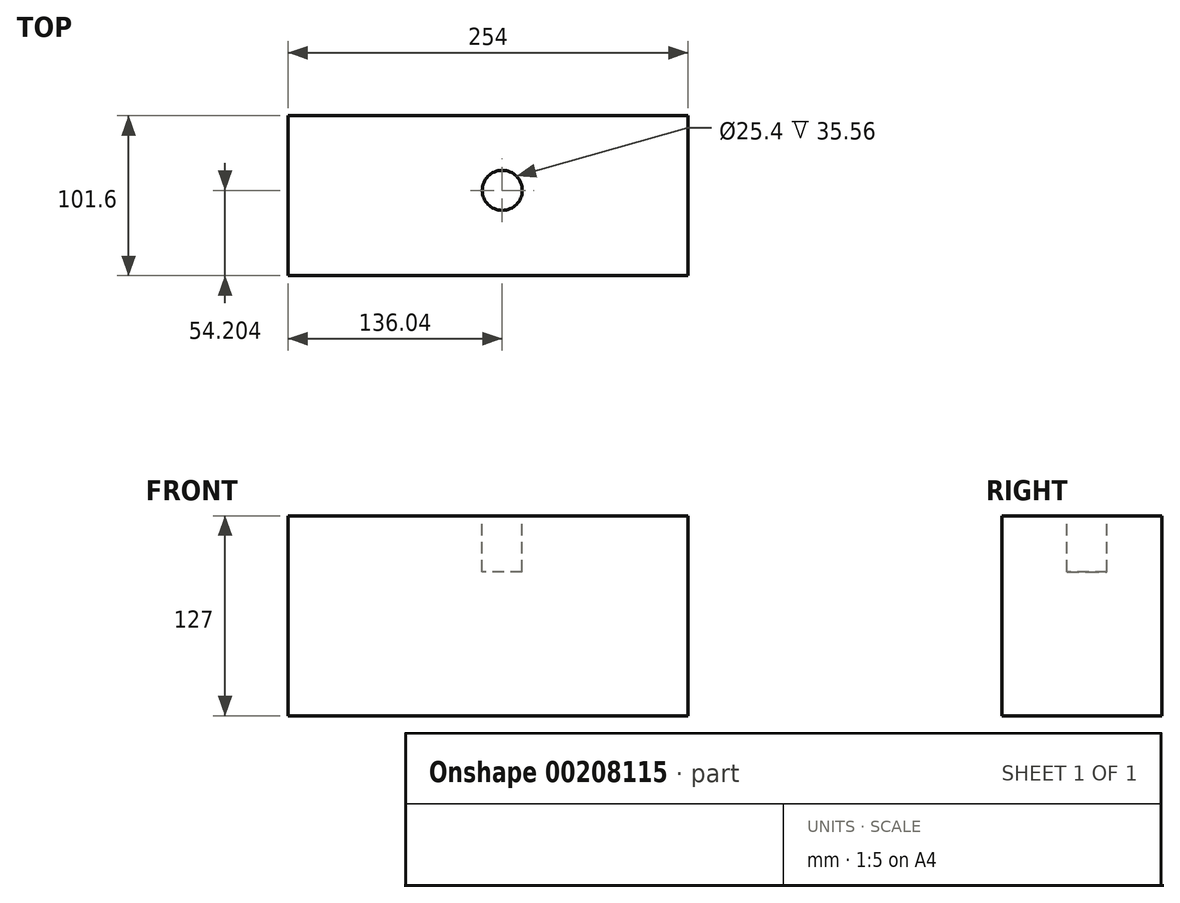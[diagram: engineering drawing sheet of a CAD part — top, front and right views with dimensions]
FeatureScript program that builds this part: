
annotation { "Feature Type Name" : "Feature", "Feature Type Description" : "" }
export const myFeature = defineFeature(function(context is Context, id is Id, definition is map)
    precondition{}
    {
        {
            var Q0;
            Q0=qCreatedBy(makeId("Top.planeOp"),FACE);
            var sketch = newSketch(context, id + "F0", { "sketchPlane" : qUnion([Q0])});
            skLineSegment(sketch, "E0.bottom", {"start": v(-214.22, -77.26) * mm, "end": v(39.78, -77.26) * mm});
            skLineSegment(sketch, "E0.top", {"start": v(-214.22, -178.86) * mm, "end": v(39.78, -178.86) * mm});
            skLineSegment(sketch, "E0.left", {"start": v(-214.22, -77.26) * mm, "end": v(-214.22, -178.86) * mm});
            skLineSegment(sketch, "E0.right", {"start": v(39.78, -77.26) * mm, "end": v(39.78, -178.86) * mm});
            skLineSegment(sketch, "E1.bottom", {"start": v(-9.04, 73.66) * mm, "end": v(41.76, 73.66) * mm});
            skLineSegment(sketch, "E1.top", {"start": v(-9.04, 200.66) * mm, "end": v(41.76, 200.66) * mm});
            skLineSegment(sketch, "E1.left", {"start": v(-9.04, 73.66) * mm, "end": v(-9.04, 200.66) * mm});
            skLineSegment(sketch, "E1.right", {"start": v(41.76, 73.66) * mm, "end": v(41.76, 200.66) * mm});
            skSolve(sketch);
        }
        {
            var Q0;
            Q0=makeQuery(id+"F0.imprint","IMPRINT",FACE,{"disambiguationData":[TD([[makeQuery(id+"F0.imprint","IMPRINT",EDGE,{"derivedFrom":sQuery(id+"F0.wireOp",EDGE,"E0.bottom")}),-1.0]])]});
            extrude(context, id + "F1", {"entities" : qUnion([Q0]), "depth" : 127 * mm});
        }
        {
            var Q0;
            Q0=makeQuery(id+"F1.opExtrude","CAP_FACE",FACE,{"disambiguationData":[OSD([sQuery(id+"F0.wireOp",EDGE,"E0.bottom"),sQuery(id+"F0.wireOp",EDGE,"E0.top"),sQuery(id+"F0.wireOp",EDGE,"E0.left"),sQuery(id+"F0.wireOp",EDGE,"E0.right")])],"isStart":false});
            var sketch = newSketch(context, id + "F2", { "sketchPlane" : qUnion([Q0])});
            skCircle(sketch, "E2", {"center": v(-78.18, -124.66) * mm, "radius": 12.7 * mm});
            skSolve(sketch);
        }
        {
            var Q0;
            Q0 = qSketchRegion(id + "F2", true);
            extrude(context, id + "F3", {"entities" : qUnion([Q0]), "operationType" : NewBodyOperationType.REMOVE, "oppositeDirection" : true, "depth" : 35.56 * mm});
        }
    });
